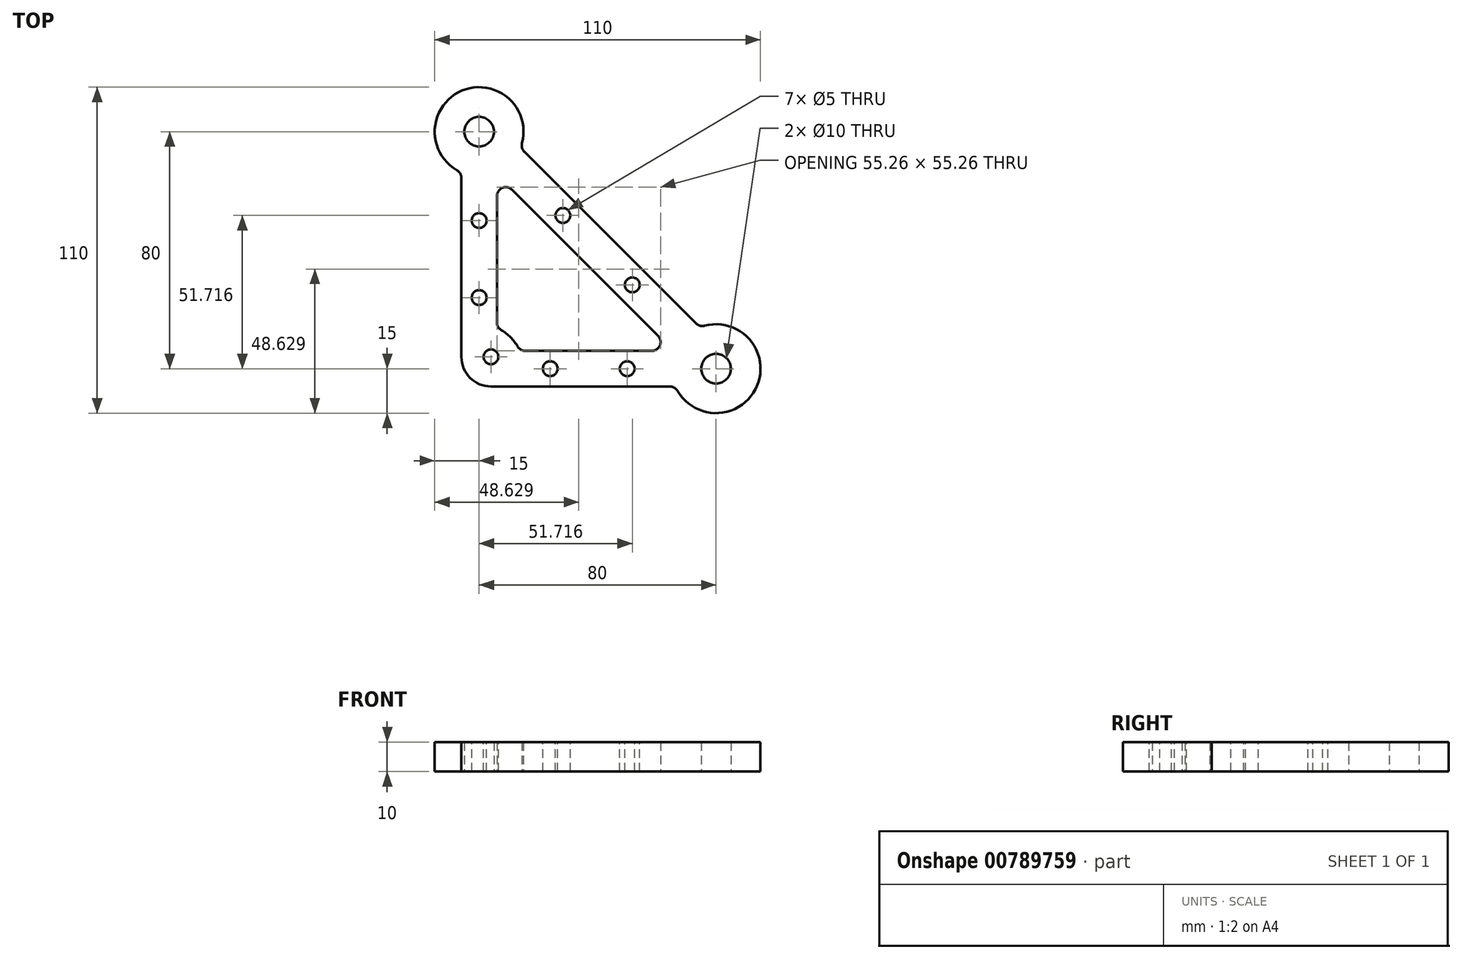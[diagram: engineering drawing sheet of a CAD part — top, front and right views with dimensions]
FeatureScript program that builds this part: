
annotation { "Feature Type Name" : "Feature", "Feature Type Description" : "" }
export const myFeature = defineFeature(function(context is Context, id is Id, definition is map)
    precondition{}
    {
        {
            var Q0;
            Q0=qCreatedBy(makeId("Top.planeOp"),FACE);
            var sketch = newSketch(context, id + "F0", { "sketchPlane" : qUnion([Q0])});
            skArc(sketch, "E0", {"start": v(66.25, -6) * mm, "mid": v(93.86, -5.74) * mm, "end": v(74.52, 13.96) * mm});
            skCircle(sketch, "E1", {"center": v(0, 80) * mm, "radius": 5 * mm});
            skCircle(sketch, "E2", {"center": v(80, 0) * mm, "radius": 5 * mm});
            skLineSegment(sketch, "E3", {"start": v(0, 80) * mm, "end": v(80, 0) * mm, "construction": true});
            skLineSegment(sketch, "E4", {"start": v(0, 80) * mm, "end": v(0, 0) * mm, "construction": true});
            skLineSegment(sketch, "E5", {"start": v(0, 0) * mm, "end": v(80, 0) * mm, "construction": true});
            skCircle(sketch, "E6", {"center": v(24, 0) * mm, "radius": 2.5 * mm, "construction": true});
            skCircle(sketch, "E7", {"center": v(50, 0) * mm, "radius": 2.5 * mm, "construction": true});
            skCircle(sketch, "E8", {"center": v(28.28, 51.72) * mm, "radius": 2.5 * mm, "construction": true});
            skCircle(sketch, "E9", {"center": v(51.72, 28.28) * mm, "radius": 2.5 * mm, "construction": true});
            skCircle(sketch, "E10", {"center": v(0, 50) * mm, "radius": 2.5 * mm, "construction": true});
            skCircle(sketch, "E11", {"center": v(0, 24) * mm, "radius": 2.5 * mm, "construction": true});
            skLineSegment(sketch, "E12.0", {"start": v(-6, 66.25) * mm, "end": v(-6, -6) * mm});
            skLineSegment(sketch, "E13.0", {"start": v(13.75, 6) * mm, "end": v(65.51, 6) * mm});
            skLineSegment(sketch, "E14.0", {"start": v(-6, -6) * mm, "end": v(66.25, -6) * mm});
            skLineSegment(sketch, "E15.trimOffspring", {"start": v(6, 65.51) * mm, "end": v(6, 13.75) * mm});
            skLineSegment(sketch, "E16.0", {"start": v(13.96, 74.52) * mm, "end": v(74.52, 13.96) * mm});
            skLineSegment(sketch, "E17.trimOffspring", {"start": v(6, 65.51) * mm, "end": v(65.51, 6) * mm});
            skArc(sketch, "E18.trimOffspring", {"start": v(13.96, 74.52) * mm, "mid": v(-5.74, 93.86) * mm, "end": v(-6, 66.25) * mm});
            skPoint(sketch, "E19", {"position": v(4, 4) * mm});
            skArc(sketch, "E20", {"start": v(13.75, 6) * mm, "mid": v(10.6, 10.6) * mm, "end": v(6, 13.75) * mm});
            skSolve(sketch);
        }
        {
            var Q0;
            Q0=makeQuery(id+"F0.imprint","IMPRINT",FACE,{"disambiguationData":[TD([[makeQuery(id+"F0.imprint","IMPRINT",EDGE,{"derivedFrom":sQuery(id+"F0.wireOp",EDGE,"E0")}),1.0]])]});
            extrude(context, id + "F1", {"entities" : qUnion([Q0]), "depth" : 10 * mm, "offsetDistance" : 25 * mm});
        }
        {
            var Q0;
            Q0=makeQuery(id+"F1.opExtrude","SWEPT_EDGE",EDGE,{"disambiguationData":[OSD([sQuery(id+"F0.wireOp",EDGE,"E12.0"),sQuery(id+"F0.wireOp",EDGE,"E14.0")])]});
            fillet(context, id + "F2", {"entities" : qUnion([Q0]), "radius" : 10 * mm, "tangentPropagation" : true, "allowEdgeOverflow" : false});
        }
        {
            var Q0;
            Q0=makeQuery(id+"F1.opExtrude","SWEPT_EDGE",EDGE,{"disambiguationData":[OSD([sQuery(id+"F0.wireOp",EDGE,"E16.0"),sQuery(id+"F0.wireOp",EDGE,"E18.trimOffspring")])]});
            var Q1;
            Q1=makeQuery(id+"F1.opExtrude","SWEPT_EDGE",EDGE,{"disambiguationData":[OSD([sQuery(id+"F0.wireOp",EDGE,"E0"),sQuery(id+"F0.wireOp",EDGE,"E16.0")])]});
            var Q2;
            Q2=makeQuery(id+"F1.opExtrude","SWEPT_EDGE",EDGE,{"disambiguationData":[OSD([sQuery(id+"F0.wireOp",EDGE,"E0"),sQuery(id+"F0.wireOp",EDGE,"E14.0")])]});
            var Q3;
            Q3=makeQuery(id+"F1.opExtrude","SWEPT_EDGE",EDGE,{"disambiguationData":[OSD([sQuery(id+"F0.wireOp",EDGE,"E12.0"),sQuery(id+"F0.wireOp",EDGE,"E18.trimOffspring")])]});
            var Q4;
            Q4=makeQuery(id+"F1.opExtrude","SWEPT_EDGE",EDGE,{"disambiguationData":[OSD([sQuery(id+"F0.wireOp",EDGE,"E13.0"),sQuery(id+"F0.wireOp",EDGE,"E17.trimOffspring")])]});
            var Q5;
            Q5=makeQuery(id+"F1.opExtrude","SWEPT_EDGE",EDGE,{"disambiguationData":[OSD([sQuery(id+"F0.wireOp",EDGE,"E15.trimOffspring"),sQuery(id+"F0.wireOp",EDGE,"E17.trimOffspring")])]});
            var Q6;
            Q6=makeQuery(id+"F1.opExtrude","SWEPT_EDGE",EDGE,{"disambiguationData":[OSD([sQuery(id+"F0.wireOp",EDGE,"E15.trimOffspring"),sQuery(id+"F0.wireOp",EDGE,"E20")])]});
            var Q7;
            Q7=makeQuery(id+"F1.opExtrude","SWEPT_EDGE",EDGE,{"disambiguationData":[OSD([sQuery(id+"F0.wireOp",EDGE,"E13.0"),sQuery(id+"F0.wireOp",EDGE,"E20")])]});
            fillet(context, id + "F3", {"entities" : qUnion([Q0, Q1, Q2, Q3, Q4, Q5, Q6, Q7]), "radius" : 3 * mm, "tangentPropagation" : true, "allowEdgeOverflow" : false});
        }
        {
            var Q0;
            Q0=makeQuery(id+"F1.opExtrude","CAP_FACE",FACE,{"disambiguationData":[OSD([sQuery(id+"F0.wireOp",EDGE,"E0"),sQuery(id+"F0.wireOp",EDGE,"E1"),sQuery(id+"F0.wireOp",EDGE,"E2"),sQuery(id+"F0.wireOp",EDGE,"E12.0"),sQuery(id+"F0.wireOp",EDGE,"E13.0"),sQuery(id+"F0.wireOp",EDGE,"E14.0"),sQuery(id+"F0.wireOp",EDGE,"E15.trimOffspring"),sQuery(id+"F0.wireOp",EDGE,"E16.0"),sQuery(id+"F0.wireOp",EDGE,"E17.trimOffspring"),sQuery(id+"F0.wireOp",EDGE,"E18.trimOffspring")])],"isStart":false});
            var sketch = newSketch(context, id + "F4", { "sketchPlane" : qUnion([Q0])});
            skPoint(sketch, "E21", {"position": v(28.28, 51.72) * mm});
            skPoint(sketch, "E22", {"position": v(51.72, 28.28) * mm});
            skPoint(sketch, "E23", {"position": v(50, 0) * mm});
            skPoint(sketch, "E24", {"position": v(24, 0) * mm});
            skPoint(sketch, "E25", {"position": v(0, 24) * mm});
            skPoint(sketch, "E26", {"position": v(0, 50) * mm});
            skPoint(sketch, "E27", {"position": v(0, 80) * mm});
            skPoint(sketch, "E28", {"position": v(80, 0) * mm});
            skPoint(sketch, "E29", {"position": v(4, 4) * mm});
            skSolve(sketch);
        }
        {
            var Q0;
            Q0=sQuery(id+"F4.wireOp",VERTEX,"E26");
            var Q1;
            Q1=sQuery(id+"F4.wireOp",VERTEX,"E25");
            var Q2;
            Q2=sQuery(id+"F4.wireOp",VERTEX,"E21");
            var Q3;
            Q3=sQuery(id+"F4.wireOp",VERTEX,"E22");
            var Q4;
            Q4=sQuery(id+"F4.wireOp",VERTEX,"E23");
            var Q5;
            Q5=sQuery(id+"F4.wireOp",VERTEX,"E24");
            var Q6;
            Q6=sQuery(id+"F4.wireOp",VERTEX,"E29");
            var Q7;
            Q7=makeQuery(id+"F1.opExtrude","SWEPT_BODY",BODY,{"disambiguationData":[OSD([sQuery(id+"F0.wireOp",EDGE,"E0"),sQuery(id+"F0.wireOp",EDGE,"E1"),sQuery(id+"F0.wireOp",EDGE,"E2"),sQuery(id+"F0.wireOp",EDGE,"E12.0"),sQuery(id+"F0.wireOp",EDGE,"E13.0"),sQuery(id+"F0.wireOp",EDGE,"E14.0"),sQuery(id+"F0.wireOp",EDGE,"E15.trimOffspring"),sQuery(id+"F0.wireOp",EDGE,"E16.0"),sQuery(id+"F0.wireOp",EDGE,"E17.trimOffspring"),sQuery(id+"F0.wireOp",EDGE,"E18.trimOffspring")])]});
            hole(context, id + "F5", {"style" : HoleStyle.SIMPLE, "endStyle" : HoleEndStyle.THROUGH, "holeDiameter" : 5 * mm, "majorDiameter" : 5 * mm, "isTappedThrough" : true, "tappedDepth" : 12 * mm, "tapClearance" : 3, "locations" : qUnion([Q0, Q1, Q2, Q3, Q4, Q5, Q6]), "scope" : qUnion([Q7])});
        }
    });
